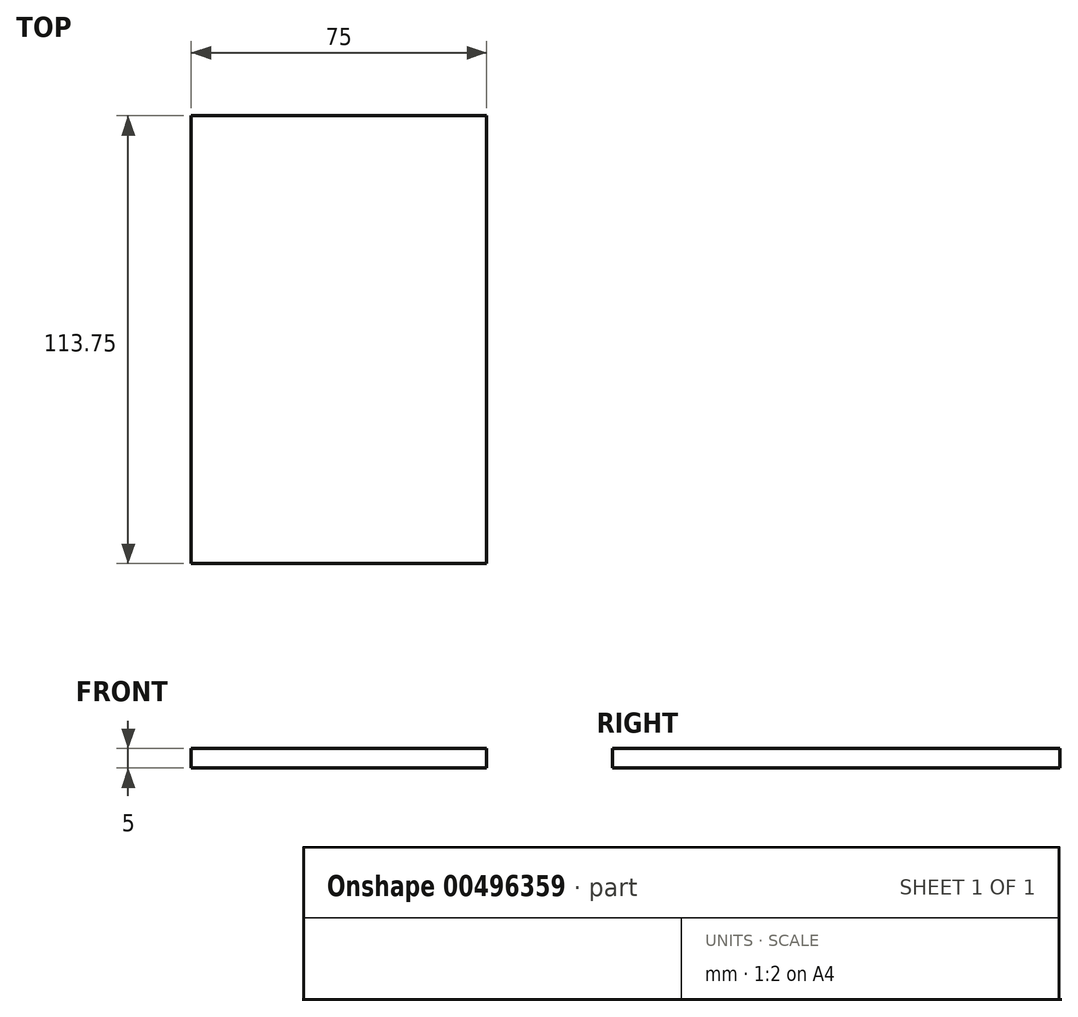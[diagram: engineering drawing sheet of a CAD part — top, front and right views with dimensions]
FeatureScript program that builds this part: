
annotation { "Feature Type Name" : "Feature", "Feature Type Description" : "" }
export const myFeature = defineFeature(function(context is Context, id is Id, definition is map)
    precondition{}
    {
        {
            var Q0;
            Q0=qCreatedBy(makeId("Top.planeOp"),FACE);
            var sketch = newSketch(context, id + "F0", { "sketchPlane" : qUnion([Q0])});
            skLineSegment(sketch, "E0.bottom", {"start": v(-50.52, 52.74) * mm, "end": v(24.48, 52.74) * mm});
            skLineSegment(sketch, "E0.top", {"start": v(-50.52, -61.01) * mm, "end": v(24.48, -61.01) * mm});
            skLineSegment(sketch, "E0.left", {"start": v(-50.52, 52.74) * mm, "end": v(-50.52, -61.01) * mm});
            skLineSegment(sketch, "E0.right", {"start": v(24.48, 52.74) * mm, "end": v(24.48, -61.01) * mm});
            skSolve(sketch);
        }
        {
            var Q0;
            Q0=makeQuery(id+"F0.imprint","IMPRINT",FACE,{"disambiguationData":[TD([[makeQuery(id+"F0.imprint","IMPRINT",EDGE,{"derivedFrom":sQuery(id+"F0.wireOp",EDGE,"E0.bottom")}),-1.0]])]});
            extrude(context, id + "F1", {"entities" : qUnion([Q0]), "depth" : 5 * mm});
        }
    });
